# Revit family: ПКН-100А
name_source: partatom
category: Арматура трубопроводов
units: mm (PartAtom-declared; Revit-internal decimal feet)

## family parameters
Всегда вертикально = Да
На основе рабочей плоскости = Нет
Общий = Нет
При загрузке вырезать с полостями = Нет
Размер круглого соединителя = Использовать диаметр
Тип детали = Клапан - Вставляется

## types (6) — shared parameters
ADSK_Единица измерения = шт.
ADSK_Завод-изготовитель = РУП "БЕЛГАЗТЕХНИКА"
ADSK_Количество = 1
ADSK_Максимальное входное давление, МПа = 1,2
ADSK_Марка = ПКН-100А
ADSK_Масса_Текст = 48,3 кг
ADSK_Пределы настройки автоматического перекрытия подачи газа при повышении контролируемого давления, МПа = 0,003-0,03
ADSK_Пределы настройки автоматического перекрытия подачи газа при понижении контролируемого давления, МПа = 0,0003-0,003
ADSK_Тип соединения = фланцевое
ADSK_Тип управляющего сигнала = пневматический
zero-valued in all types: Отметка по умолчанию

## per-type parameters (varying)
| type | ADSK_Диапазон контролируемого давления, МПа | ADSK_Наименование | исполнение 00 | исполнение 01 |
| исполнение 00 0,0016-0,003 | 0,0016-0,003 | Клапан ПКН-100А-00  ТУ РБ 00555028-012-94 0,0016-0,003 | Да | Нет |
| исполнение 00 0,003-0,008 | 0,003-0,008 | Клапан ПКН-100А-00  ТУ РБ 00555028-012-94 0,003-0,008 | Да | Нет |
| исполнение 00 0,008-0,024 | 0,008-0,024 | Клапан ПКН-100А-00  ТУ РБ 00555028-012-94 0,008-0,024 | Да | Нет |
| исполнение 01 0,0016-0,003 | 0,0016-0,003 | Клапан ПКН-100А-01  ТУ РБ 00555028-012-94 0,0016-0,003 | Нет | Да |
| исполнение 01 0,003-0,008 | 0,003-0,008 | Клапан ПКН-100А-01  ТУ РБ 00555028-012-94 0,003-0,008 | Нет | Да |
| исполнение 01 0,008-0,024 | 0,008-0,024 | Клапан ПКН-100А-01  ТУ РБ 00555028-012-94 0,008-0,024 | Нет | Да |
